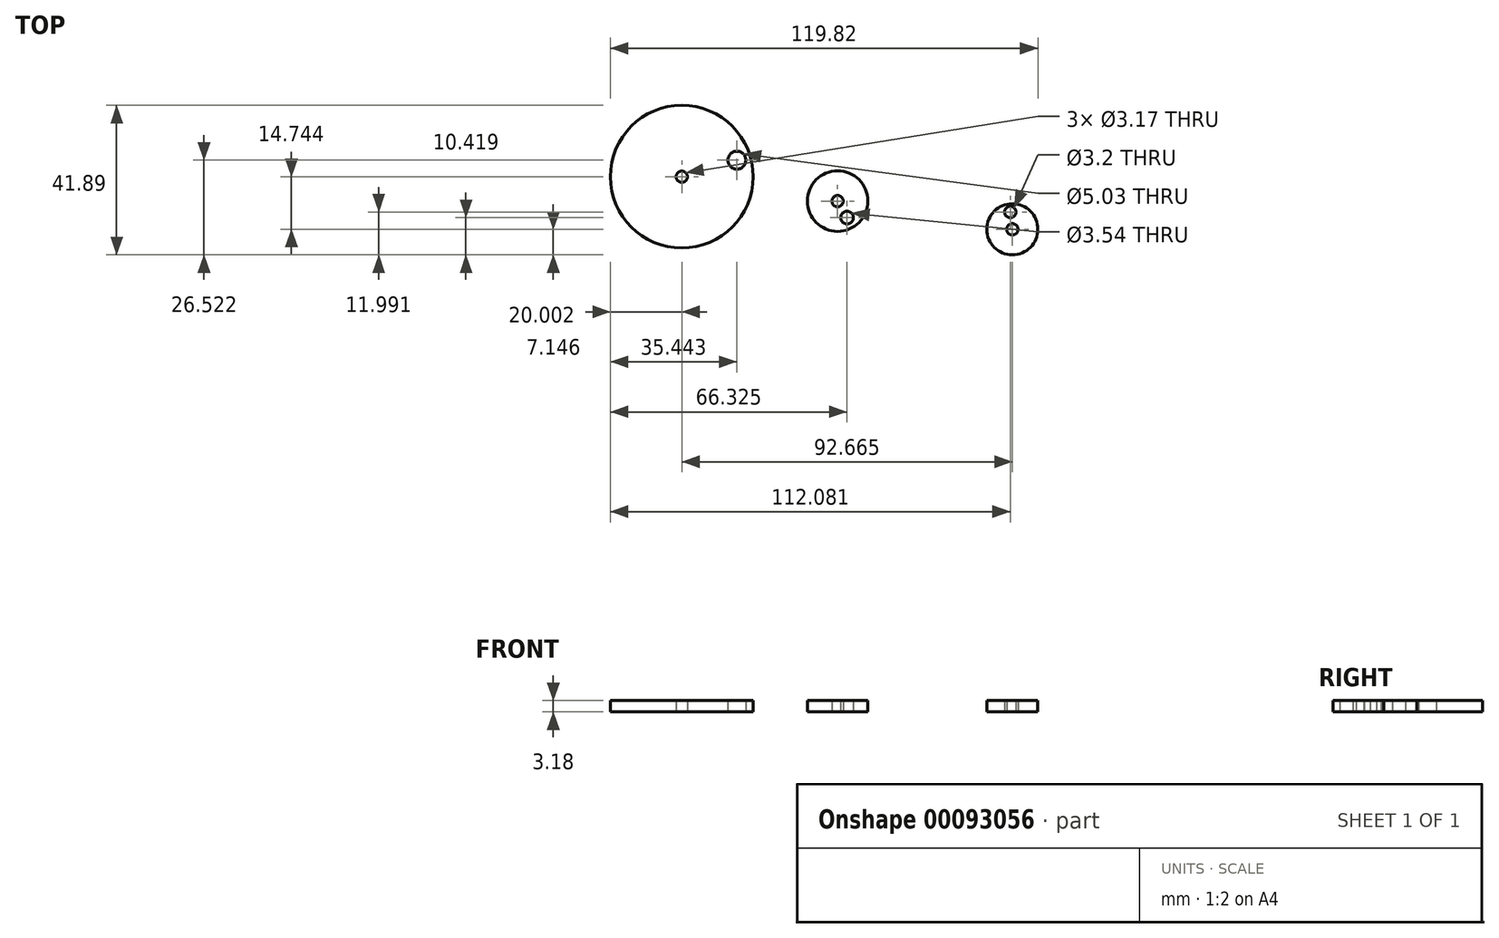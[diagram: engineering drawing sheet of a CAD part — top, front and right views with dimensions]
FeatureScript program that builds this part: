
annotation { "Feature Type Name" : "Feature", "Feature Type Description" : "" }
export const myFeature = defineFeature(function(context is Context, id is Id, definition is map)
    precondition{}
    {
        {
            var Q0;
            Q0=qCreatedBy(makeId("Top.planeOp"),FACE);
            var sketch = newSketch(context, id + "F0", { "sketchPlane" : qUnion([Q0])});
            skLineSegment(sketch, "E0.bottom", {"start": v(-133.05, 126.43) * mm, "end": v(146.35, 126.43) * mm});
            skLineSegment(sketch, "E0.top", {"start": v(-133.05, -89.47) * mm, "end": v(146.35, -89.47) * mm});
            skLineSegment(sketch, "E0.left", {"start": v(-133.05, 126.43) * mm, "end": v(-133.05, -89.47) * mm});
            skLineSegment(sketch, "E0.right", {"start": v(146.35, 126.43) * mm, "end": v(146.35, -89.47) * mm});
            skCircle(sketch, "E1", {"center": v(39.5, 8.52) * mm, "radius": 7.15 * mm});
            skCircle(sketch, "E2", {"center": v(39.5, 8.52) * mm, "radius": 1.59 * mm});
            skCircle(sketch, "E3", {"center": v(38.91, 13.36) * mm, "radius": 1.6 * mm});
            skCircle(sketch, "E4", {"center": v(-53.17, 23.26) * mm, "radius": 20 * mm});
            skCircle(sketch, "E5", {"center": v(-53.17, 23.26) * mm, "radius": 1.59 * mm});
            skCircle(sketch, "E6", {"center": v(-37.73, 27.9) * mm, "radius": 2.52 * mm});
            skCircle(sketch, "E7", {"center": v(-9.5, 16.42) * mm, "radius": 8.5 * mm});
            skCircle(sketch, "E8", {"center": v(-9.5, 16.42) * mm, "radius": 1.59 * mm});
            skCircle(sketch, "E9", {"center": v(-6.85, 11.79) * mm, "radius": 1.77 * mm});
            skSolve(sketch);
        }
        {
            var Q0;
            Q0=makeQuery(id+"F0.imprint","IMPRINT",FACE,{"disambiguationData":[TD([[makeQuery(id+"F0.imprint","IMPRINT",EDGE,{"derivedFrom":sQuery(id+"F0.wireOp",EDGE,"E7")}),1.0]])]});
            var Q1;
            Q1=makeQuery(id+"F0.imprint","IMPRINT",FACE,{"disambiguationData":[TD([[makeQuery(id+"F0.imprint","IMPRINT",EDGE,{"derivedFrom":sQuery(id+"F0.wireOp",EDGE,"E4")}),1.0]])]});
            var Q2;
            Q2=makeQuery(id+"F0.imprint","IMPRINT",FACE,{"disambiguationData":[TD([[makeQuery(id+"F0.imprint","IMPRINT",EDGE,{"derivedFrom":sQuery(id+"F0.wireOp",EDGE,"E1")}),1.0]])]});
            var Q3;
            Q3=sQuery(id+"F0.wireOp",EDGE,"E4");
            extrude(context, id + "F1", {"entities" : qUnion([Q0, Q1, Q2]), "surfaceEntities" : qUnion([Q3]), "depth" : 3.17 * mm});
        }
    });
